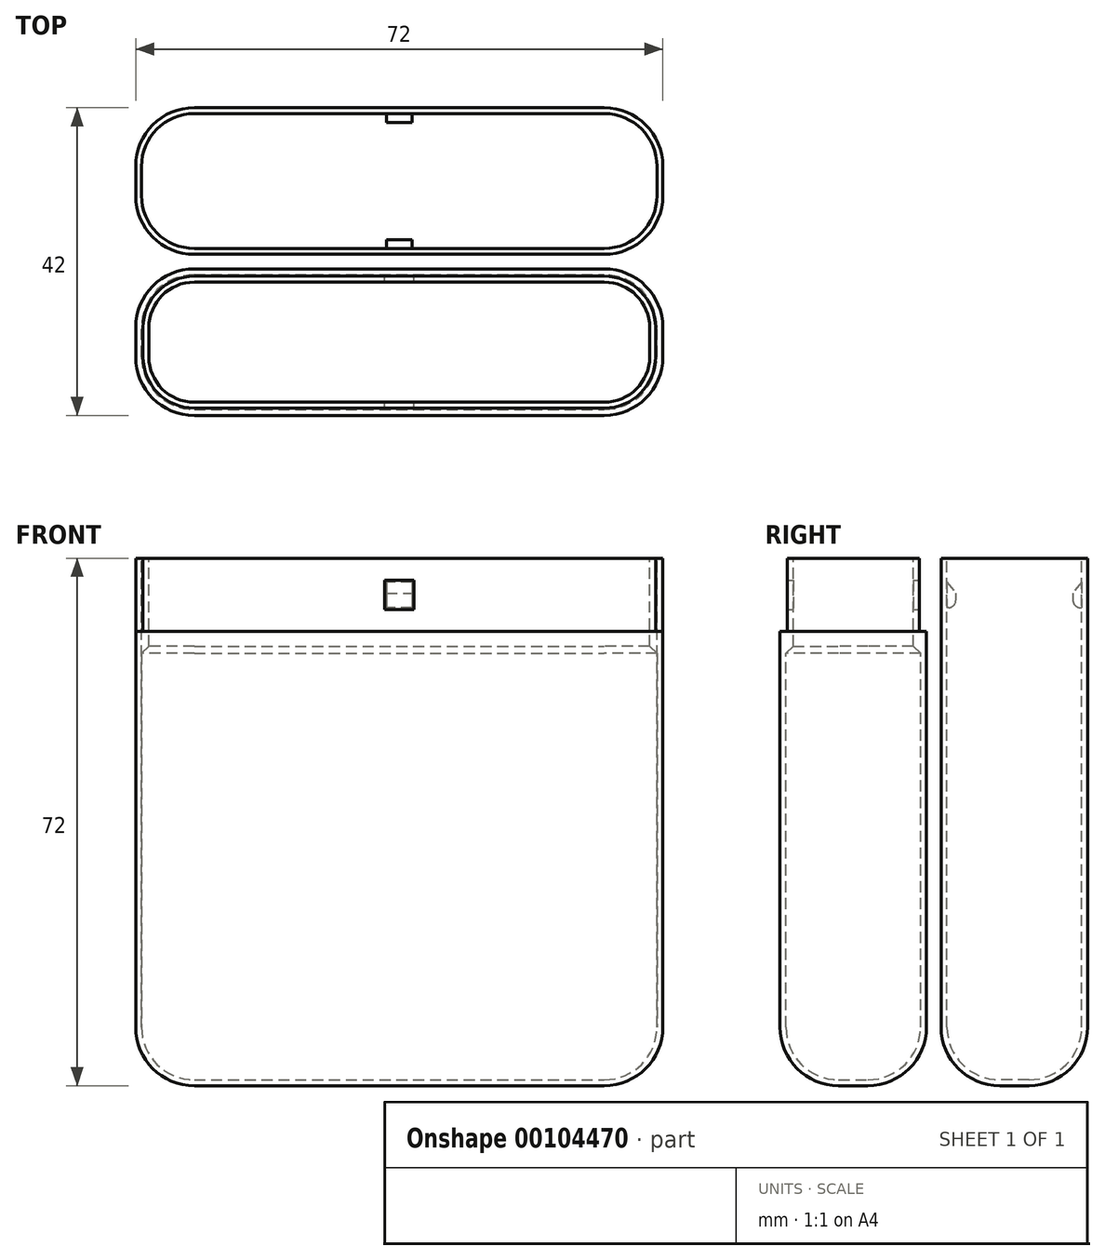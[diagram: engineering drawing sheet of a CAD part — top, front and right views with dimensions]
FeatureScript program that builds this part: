
annotation { "Feature Type Name" : "Feature", "Feature Type Description" : "" }
export const myFeature = defineFeature(function(context is Context, id is Id, definition is map)
    precondition{}
    {
        {
            var Q0;
            Q0=qCreatedBy(makeId("Top.planeOp"),FACE);
            var sketch = newSketch(context, id + "F0", { "sketchPlane" : qUnion([Q0])});
            skLineSegment(sketch, "E0.bottom", {"start": v(0, 0) * mm, "end": v(72, 0) * mm});
            skLineSegment(sketch, "E0.top", {"start": v(0, 20) * mm, "end": v(72, 20) * mm});
            skLineSegment(sketch, "E0.left", {"start": v(0, 0) * mm, "end": v(0, 20) * mm});
            skLineSegment(sketch, "E0.right", {"start": v(72, 0) * mm, "end": v(72, 20) * mm});
            skLineSegment(sketch, "E1.bottom", {"start": v(0, -2) * mm, "end": v(72, -2) * mm});
            skLineSegment(sketch, "E1.top", {"start": v(0, -22) * mm, "end": v(72, -22) * mm});
            skLineSegment(sketch, "E1.left", {"start": v(0, -2) * mm, "end": v(0, -22) * mm});
            skLineSegment(sketch, "E1.right", {"start": v(72, -2) * mm, "end": v(72, -22) * mm});
            skSolve(sketch);
        }
        {
            var Q0;
            Q0=makeQuery(id+"F0.imprint","IMPRINT",FACE,{"disambiguationData":[TD([[makeQuery(id+"F0.imprint","IMPRINT",EDGE,{"derivedFrom":sQuery(id+"F0.wireOp",EDGE,"E0.bottom")}),1.0]])]});
            var Q1;
            Q1=makeQuery(id+"F0.imprint","IMPRINT",FACE,{"disambiguationData":[TD([[makeQuery(id+"F0.imprint","IMPRINT",EDGE,{"derivedFrom":sQuery(id+"F0.wireOp",EDGE,"E1.bottom")}),-1.0]])]});
            extrude(context, id + "F1", {"entities" : qUnion([Q0, Q1]), "depth" : 72 * mm});
        }
        {
            var Q0;
            Q0=makeQuery(id+"F1.opExtrude","SWEPT_EDGE",EDGE,{"disambiguationData":[OSD([sQuery(id+"F0.wireOp",EDGE,"E0.top"),sQuery(id+"F0.wireOp",EDGE,"E0.left")])]});
            var Q1;
            Q1=makeQuery(id+"F1.opExtrude","SWEPT_EDGE",EDGE,{"disambiguationData":[OSD([sQuery(id+"F0.wireOp",EDGE,"E0.bottom"),sQuery(id+"F0.wireOp",EDGE,"E0.left")])]});
            var Q2;
            Q2=makeQuery(id+"F1.opExtrude","CAP_EDGE",EDGE,{"disambiguationData":[OSD([sQuery(id+"F0.wireOp",EDGE,"E0.left")])],"isStart":true});
            var Q3;
            Q3=makeQuery(id+"F1.opExtrude","CAP_EDGE",EDGE,{"disambiguationData":[OSD([sQuery(id+"F0.wireOp",EDGE,"E0.top")])],"isStart":true});
            var Q4;
            Q4=makeQuery(id+"F1.opExtrude","CAP_EDGE",EDGE,{"disambiguationData":[OSD([sQuery(id+"F0.wireOp",EDGE,"E0.bottom")])],"isStart":true});
            var Q5;
            Q5=makeQuery(id+"F1.opExtrude","SWEPT_EDGE",EDGE,{"disambiguationData":[OSD([sQuery(id+"F0.wireOp",EDGE,"E0.top"),sQuery(id+"F0.wireOp",EDGE,"E0.right")])]});
            var Q6;
            Q6=makeQuery(id+"F1.opExtrude","CAP_EDGE",EDGE,{"disambiguationData":[OSD([sQuery(id+"F0.wireOp",EDGE,"E0.right")])],"isStart":true});
            var Q7;
            Q7=makeQuery(id+"F1.opExtrude","SWEPT_EDGE",EDGE,{"disambiguationData":[OSD([sQuery(id+"F0.wireOp",EDGE,"E0.bottom"),sQuery(id+"F0.wireOp",EDGE,"E0.right")])]});
            var Q8;
            Q8=makeQuery(id+"F1.opExtrude","SWEPT_EDGE",EDGE,{"disambiguationData":[OSD([sQuery(id+"F0.wireOp",EDGE,"E1.bottom"),sQuery(id+"F0.wireOp",EDGE,"E1.left")])]});
            var Q9;
            Q9=makeQuery(id+"F1.opExtrude","SWEPT_EDGE",EDGE,{"disambiguationData":[OSD([sQuery(id+"F0.wireOp",EDGE,"E1.top"),sQuery(id+"F0.wireOp",EDGE,"E1.left")])]});
            var Q10;
            Q10=makeQuery(id+"F1.opExtrude","SWEPT_EDGE",EDGE,{"disambiguationData":[OSD([sQuery(id+"F0.wireOp",EDGE,"E1.top"),sQuery(id+"F0.wireOp",EDGE,"E1.right")])]});
            var Q11;
            Q11=makeQuery(id+"F1.opExtrude","SWEPT_EDGE",EDGE,{"disambiguationData":[OSD([sQuery(id+"F0.wireOp",EDGE,"E1.bottom"),sQuery(id+"F0.wireOp",EDGE,"E1.right")])]});
            var Q12;
            Q12=makeQuery(id+"F1.opExtrude","CAP_EDGE",EDGE,{"disambiguationData":[OSD([sQuery(id+"F0.wireOp",EDGE,"E1.right")])],"isStart":true});
            var Q13;
            Q13=makeQuery(id+"F1.opExtrude","CAP_EDGE",EDGE,{"disambiguationData":[OSD([sQuery(id+"F0.wireOp",EDGE,"E1.bottom")])],"isStart":true});
            var Q14;
            Q14=makeQuery(id+"F1.opExtrude","CAP_EDGE",EDGE,{"disambiguationData":[OSD([sQuery(id+"F0.wireOp",EDGE,"E1.top")])],"isStart":true});
            var Q15;
            Q15=makeQuery(id+"F1.opExtrude","CAP_EDGE",EDGE,{"disambiguationData":[OSD([sQuery(id+"F0.wireOp",EDGE,"E1.left")])],"isStart":true});
            fillet(context, id + "F2", {"entities" : qUnion([Q0, Q1, Q2, Q3, Q4, Q5, Q6, Q7, Q8, Q9, Q10, Q11, Q12, Q13, Q14, Q15]), "radius" : 8 * mm, "tangentPropagation" : true, "allowEdgeOverflow" : false});
        }
        {
            var Q0;
            Q0=makeQuery(id+"F1.opExtrude","CAP_FACE",FACE,{"disambiguationData":[OSD([sQuery(id+"F0.wireOp",EDGE,"E0.bottom"),sQuery(id+"F0.wireOp",EDGE,"E0.top"),sQuery(id+"F0.wireOp",EDGE,"E0.left"),sQuery(id+"F0.wireOp",EDGE,"E0.right")])],"isStart":false});
            var Q1;
            Q1=makeQuery(id+"F1.opExtrude","CAP_FACE",FACE,{"disambiguationData":[OSD([sQuery(id+"F0.wireOp",EDGE,"E1.bottom"),sQuery(id+"F0.wireOp",EDGE,"E1.top"),sQuery(id+"F0.wireOp",EDGE,"E1.left"),sQuery(id+"F0.wireOp",EDGE,"E1.right")])],"isStart":false});
            shell(context, id + "F3", {"entities" : qUnion([Q0, Q1]), "thickness" : 0.8 * mm});
        }
        {
            var Q0;
            {var subQ0=sQuery(id+"F0.wireOp",EDGE,"E0.bottom");Q0=makeQuery(id+"F3.opShell","OFFSET_FACE",FACE,{"disambiguationData":[OSD([subQ0]),TDD([makeQuery(id+"F1.opExtrude","SWEPT_FACE",FACE,{"disambiguationData":[OSD([subQ0])]})])]});}
            var sketch = newSketch(context, id + "F4", { "sketchPlane" : qUnion([Q0])});
            skLineSegment(sketch, "E2.bottom", {"start": v(-37.75, 68.75) * mm, "end": v(-34.25, 68.75) * mm});
            skLineSegment(sketch, "E2.top", {"start": v(-37.75, 65.25) * mm, "end": v(-34.25, 65.25) * mm});
            skLineSegment(sketch, "E2.left", {"start": v(-37.75, 68.75) * mm, "end": v(-37.75, 65.25) * mm});
            skLineSegment(sketch, "E2.right", {"start": v(-34.25, 68.75) * mm, "end": v(-34.25, 65.25) * mm});
            skPoint(sketch, "E3", {"position": v(-36, 72) * mm});
            skPoint(sketch, "E4", {"position": v(-36, 68.75) * mm});
            skSolve(sketch);
        }
        {
            var Q0;
            Q0=qSketchRegion(id+"F4",true);
            extrude(context, id + "F5", {"entities" : qUnion([Q0]), "operationType" : NewBodyOperationType.ADD, "depth" : 1.2 * mm});
        }
        {
            var Q0;
            Q0=makeQuery(id+"F5.opExtrude","CAP_EDGE",EDGE,{"disambiguationData":[OSD([sQuery(id+"F4.wireOp",EDGE,"E2.top")])],"isStart":false});
            fillet(context, id + "F6", {"entities" : qUnion([Q0]), "radius" : 1 * mm, "tangentPropagation" : true, "allowEdgeOverflow" : false});
        }
        {
            var Q0;
            Q0=makeQuery(id+"F5.opExtrude","CAP_EDGE",EDGE,{"disambiguationData":[OSD([sQuery(id+"F4.wireOp",EDGE,"E2.bottom")])],"isStart":false});
            chamfer(context, id + "F7", {"entities" : qUnion([Q0]), "chamferType" : ChamferType.TWO_OFFSETS, "width1" : 1.2 * mm, "oppositeDirection" : false, "width2" : 1.5 * mm, "tangentPropagation" : true});
        }
        {
            var Q0;
            {var subQ0=sQuery(id+"F0.wireOp",EDGE,"E0.top");Q0=makeQuery(id+"F3.opShell","OFFSET_FACE",FACE,{"disambiguationData":[OSD([subQ0]),TDD([makeQuery(id+"F1.opExtrude","SWEPT_FACE",FACE,{"disambiguationData":[OSD([subQ0])]})])]});}
            var Q1;
            {var subQ0=sQuery(id+"F0.wireOp",EDGE,"E0.bottom");Q1=makeQuery(id+"F3.opShell","OFFSET_FACE",FACE,{"disambiguationData":[OSD([subQ0]),TDD([makeQuery(id+"F1.opExtrude","SWEPT_FACE",FACE,{"disambiguationData":[OSD([subQ0])]})])]});}
            cPlane(context, id + "F8", {"entities" : qUnion([Q0, Q1]), "cplaneType" : CPlaneType.MID_PLANE, "offset" : 150 * mm, "width" : 150 * mm, "height" : 150 * mm});
        }
        {
            var Q0;
            Q0=makeQuery(id+"F1.opExtrude","SWEPT_BODY",BODY,{"disambiguationData":[OSD([sQuery(id+"F0.wireOp",EDGE,"E0.bottom"),sQuery(id+"F0.wireOp",EDGE,"E0.top"),sQuery(id+"F0.wireOp",EDGE,"E0.left"),sQuery(id+"F0.wireOp",EDGE,"E0.right")])]});
            var Q1;
            Q1=qCreatedBy(id+"F8.planeOp",FACE);
            mirror(context, id + "F9", {"operationType" : NewBodyOperationType.ADD, "entities" : qUnion([Q0]), "mirrorPlane" : qUnion([Q1])});
        }
        {
            var Q0;
            Q0=makeQuery(id+"F1.opExtrude","CAP_FACE",FACE,{"disambiguationData":[OSD([sQuery(id+"F0.wireOp",EDGE,"E1.bottom"),sQuery(id+"F0.wireOp",EDGE,"E1.top"),sQuery(id+"F0.wireOp",EDGE,"E1.left"),sQuery(id+"F0.wireOp",EDGE,"E1.right")])],"isStart":false});
            extrude(context, id + "F10", {"entities" : qUnion([Q0]), "operationType" : NewBodyOperationType.REMOVE, "oppositeDirection" : true, "depth" : 10 * mm});
        }
        {
            var Q0;
            Q0=makeQuery(id+"F10.boolean.opBoolean","COPY",FACE,{"derivedFrom":makeQuery(id+"F10.opExtrude","CAP_FACE",FACE,{"disambiguationData":[OSD([sQuery(id+"F0.wireOp",EDGE,"E1.bottom"),sQuery(id+"F0.wireOp",EDGE,"E1.top"),sQuery(id+"F0.wireOp",EDGE,"E1.left"),sQuery(id+"F0.wireOp",EDGE,"E1.right")])],"isStart":false})});
            var sketch = newSketch(context, id + "F11", { "sketchPlane" : qUnion([Q0])});
            skLineSegment(sketch, "E5.0", {"start": v(8, -3.8) * mm, "end": v(64, -3.8) * mm});
            skArc(sketch, "E5.1", {"start": v(70.2, -10) * mm, "mid": v(68.38, -5.62) * mm, "end": v(64, -3.8) * mm});
            skArc(sketch, "E5.2", {"start": v(8, -3.8) * mm, "mid": v(3.62, -5.62) * mm, "end": v(1.8, -10) * mm});
            skLineSegment(sketch, "E5.3", {"start": v(70.2, -10) * mm, "end": v(70.2, -14) * mm});
            skLineSegment(sketch, "E5.4", {"start": v(1.8, -10) * mm, "end": v(1.8, -14) * mm});
            skArc(sketch, "E5.5", {"start": v(1.8, -14) * mm, "mid": v(3.62, -18.38) * mm, "end": v(8, -20.2) * mm});
            skLineSegment(sketch, "E5.6", {"start": v(8, -20.2) * mm, "end": v(64, -20.2) * mm});
            skArc(sketch, "E5.7", {"start": v(64, -20.2) * mm, "mid": v(68.38, -18.38) * mm, "end": v(70.2, -14) * mm});
            skSolve(sketch);
        }
        {
            var Q0;
            Q0=makeQuery(id+"F11.imprint","IMPRINT",FACE,{"disambiguationData":[TD([[makeQuery(id+"F11.imprint","IMPRINT",EDGE,{"derivedFrom":sQuery(id+"F11.wireOp",EDGE,"E5.0")}),1.0]])]});
            var Q1;
            {var subQ3=sQuery(id+"F0.wireOp",EDGE,"E1.bottom");var subQ10=makeQuery(id+"F1.opExtrude","CAP_EDGE",EDGE,{"disambiguationData":[OSD([subQ3])],"isStart":false});Q1=makeQuery(id+"F11.imprint","IMPRINT",FACE,{"disambiguationData":[TD([[makeQuery(id+"F11.imprint","IMPRINT",EDGE,{"derivedFrom":makeQuery(id+"F10.boolean.opBoolean","COPY",EDGE,{"derivedFrom":makeQuery(id+"F10.opExtrude","CAP_EDGE",EDGE,{"disambiguationData":[OSD([subQ3]),TDD([subQ10])],"isStart":false})})}),-1.0]])]});}
            extrude(context, id + "F12", {"entities" : qUnion([Q0, Q1]), "operationType" : NewBodyOperationType.ADD, "oppositeDirection" : true, "depth" : 3 * mm});
        }
        {
            var Q0;
            {var subQ0=sQuery(id+"F0.wireOp",EDGE,"E1.right");var subQ1=sQuery(id+"F0.wireOp",EDGE,"E1.left");var subQ2=sQuery(id+"F0.wireOp",EDGE,"E1.top");var subQ3=sQuery(id+"F0.wireOp",EDGE,"E1.bottom");Q0=makeQuery(id+"F12.boolean.opBoolean","MERGE",FACE,{"derivedFrom":[makeQuery(id+"F10.boolean.opBoolean","COPY",FACE,{"derivedFrom":makeQuery(id+"F10.opExtrude","CAP_FACE",FACE,{"disambiguationData":[OSD([subQ3,subQ2,subQ1,subQ0])],"isStart":false})}),makeQuery(id+"F12.opExtrude","CAP_FACE",FACE,{"disambiguationData":[OSD([subQ3,subQ2,subQ1,subQ0,sQuery(id+"F11.wireOp",EDGE,"E5.0"),sQuery(id+"F11.wireOp",EDGE,"E5.1"),sQuery(id+"F11.wireOp",EDGE,"E5.2"),sQuery(id+"F11.wireOp",EDGE,"E5.3"),sQuery(id+"F11.wireOp",EDGE,"E5.4"),sQuery(id+"F11.wireOp",EDGE,"E5.5"),sQuery(id+"F11.wireOp",EDGE,"E5.6"),sQuery(id+"F11.wireOp",EDGE,"E5.7")])],"isStart":true})]});}
            var sketch = newSketch(context, id + "F13", { "sketchPlane" : qUnion([Q0])});
            skLineSegment(sketch, "E6.0", {"start": v(8, -3) * mm, "end": v(64, -3) * mm});
            skArc(sketch, "E6.1", {"start": v(71, -10) * mm, "mid": v(68.95, -5.05) * mm, "end": v(64, -3) * mm});
            skArc(sketch, "E6.2", {"start": v(8, -3) * mm, "mid": v(3.05, -5.05) * mm, "end": v(1, -10) * mm});
            skLineSegment(sketch, "E6.3", {"start": v(71, -10) * mm, "end": v(71, -14) * mm});
            skLineSegment(sketch, "E6.4", {"start": v(1, -10) * mm, "end": v(1, -14) * mm});
            skArc(sketch, "E6.5", {"start": v(1, -14) * mm, "mid": v(3.05, -18.95) * mm, "end": v(8, -21) * mm});
            skLineSegment(sketch, "E6.6", {"start": v(8, -21) * mm, "end": v(64, -21) * mm});
            skArc(sketch, "E6.7", {"start": v(64, -21) * mm, "mid": v(68.95, -18.95) * mm, "end": v(71, -14) * mm});
            skArc(sketch, "E7.0", {"start": v(8, -3.8) * mm, "mid": v(3.62, -5.62) * mm, "end": v(1.8, -10) * mm});
            skLineSegment(sketch, "E7.1", {"start": v(8, -3.8) * mm, "end": v(64, -3.8) * mm});
            skArc(sketch, "E7.2", {"start": v(70.2, -10) * mm, "mid": v(68.38, -5.62) * mm, "end": v(64, -3.8) * mm});
            skLineSegment(sketch, "E7.3", {"start": v(70.2, -10) * mm, "end": v(70.2, -14) * mm});
            skArc(sketch, "E7.4", {"start": v(64, -20.2) * mm, "mid": v(68.38, -18.38) * mm, "end": v(70.2, -14) * mm});
            skLineSegment(sketch, "E7.5", {"start": v(8, -20.2) * mm, "end": v(64, -20.2) * mm});
            skArc(sketch, "E7.6", {"start": v(1.8, -14) * mm, "mid": v(3.62, -18.38) * mm, "end": v(8, -20.2) * mm});
            skLineSegment(sketch, "E7.7", {"start": v(1.8, -10) * mm, "end": v(1.8, -14) * mm});
            skSolve(sketch);
        }
        {
            var Q0;
            Q0=makeQuery(id+"F13.imprint","IMPRINT",FACE,{"disambiguationData":[TD([[makeQuery(id+"F13.imprint","IMPRINT",EDGE,{"derivedFrom":sQuery(id+"F13.wireOp",EDGE,"E6.0")}),-1.0]])]});
            extrude(context, id + "F14", {"entities" : qUnion([Q0]), "operationType" : NewBodyOperationType.ADD, "depth" : 10 * mm});
        }
        {
            var Q0;
            Q0=makeQuery(id+"F14.opExtrude","SWEPT_FACE",FACE,{"disambiguationData":[OSD([sQuery(id+"F13.wireOp",EDGE,"E6.0")])]});
            var sketch = newSketch(context, id + "F15", { "sketchPlane" : qUnion([Q0])});
            skPoint(sketch, "E8.oppositeSnap0", {"position": v(-8, 67) * mm});
            skPoint(sketch, "E9", {"position": v(-36, 72) * mm});
            skPoint(sketch, "E10", {"position": v(-36, 69) * mm});
            skLineSegment(sketch, "E11.bottom", {"start": v(-34, 65) * mm, "end": v(-38, 65) * mm});
            skLineSegment(sketch, "E11.top", {"start": v(-34, 69) * mm, "end": v(-38, 69) * mm});
            skLineSegment(sketch, "E11.left", {"start": v(-34, 65) * mm, "end": v(-34, 69) * mm});
            skLineSegment(sketch, "E11.right", {"start": v(-38, 65) * mm, "end": v(-38, 69) * mm});
            skSolve(sketch);
        }
        {
            var Q0;
            Q0=makeQuery(id+"F15.imprint","IMPRINT",FACE,{"disambiguationData":[TD([[makeQuery(id+"F15.imprint","IMPRINT",EDGE,{"derivedFrom":sQuery(id+"F15.wireOp",EDGE,"E11.bottom")}),-1.0]])]});
            extrude(context, id + "F16", {"entities" : qUnion([Q0]), "operationType" : NewBodyOperationType.REMOVE, "oppositeDirection" : true, "depth" : 25 * mm});
        }
        {
            var Q0;
            Q0=makeQuery(id+"F12.opExtrude","CAP_EDGE",EDGE,{"disambiguationData":[OSD([sQuery(id+"F11.wireOp",EDGE,"E5.6")])],"isStart":false});
            chamfer(context, id + "F17", {"entities" : qUnion([Q0]), "width" : 1 * mm, "tangentPropagation" : true});
        }
    });
